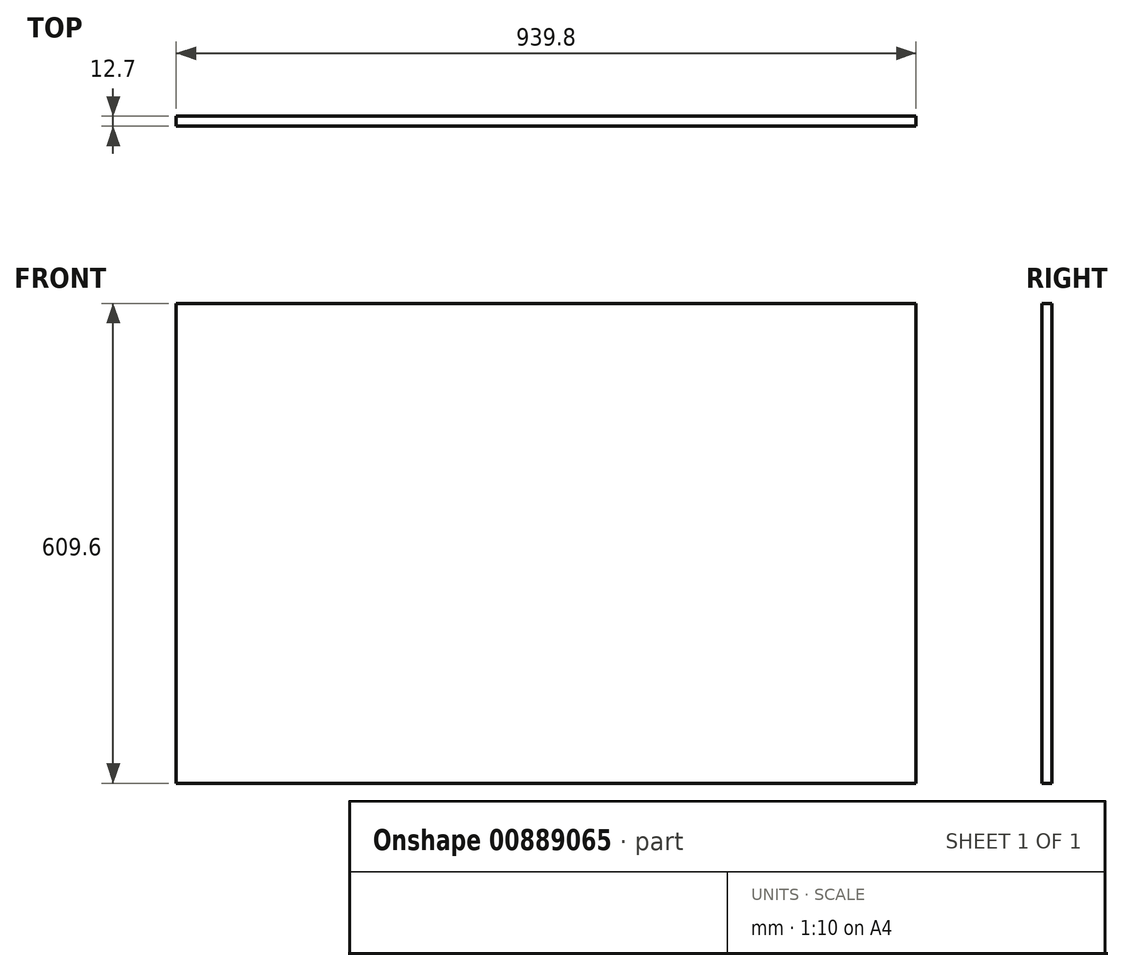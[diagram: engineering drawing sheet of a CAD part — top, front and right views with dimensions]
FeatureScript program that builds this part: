
annotation { "Feature Type Name" : "Feature", "Feature Type Description" : "" }
export const myFeature = defineFeature(function(context is Context, id is Id, definition is map)
    precondition{}
    {
        {
            var Q0;
            Q0=qCreatedBy(makeId("Front.planeOp"),FACE);
            var sketch = newSketch(context, id + "F0", { "sketchPlane" : qUnion([Q0])});
            skLineSegment(sketch, "E0.bottom", {"start": v(-469.9, 304.8) * mm, "end": v(469.9, 304.8) * mm});
            skLineSegment(sketch, "E0.top", {"start": v(-469.9, -304.8) * mm, "end": v(469.9, -304.8) * mm});
            skLineSegment(sketch, "E0.left", {"start": v(-469.9, 304.8) * mm, "end": v(-469.9, -304.8) * mm});
            skLineSegment(sketch, "E0.right", {"start": v(469.9, 304.8) * mm, "end": v(469.9, -304.8) * mm});
            skPoint(sketch, "E0.middle", {"position": v(0, 0) * mm});
            skSolve(sketch);
        }
        {
            var Q0;
            Q0 = qSketchRegion(id + "F0", true);
            extrude(context, id + "F1", {"entities" : qUnion([Q0]), "depth" : 12.7 * mm, "offsetDistance" : 25.4 * mm});
        }
    });
